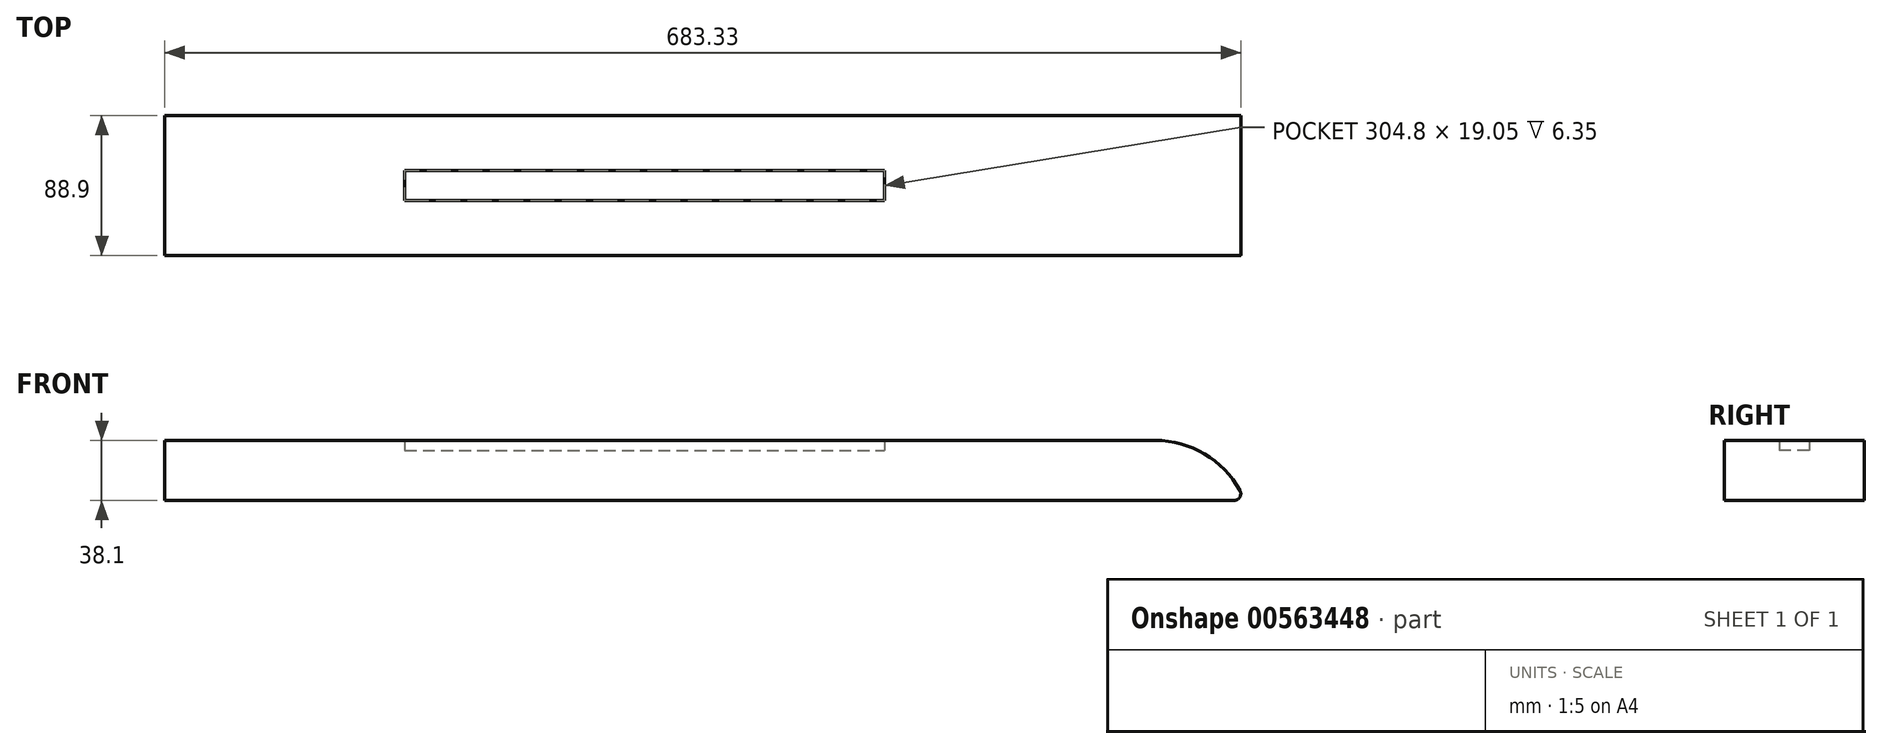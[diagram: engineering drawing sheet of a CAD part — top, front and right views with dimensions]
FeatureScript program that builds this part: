
annotation { "Feature Type Name" : "Feature", "Feature Type Description" : "" }
export const myFeature = defineFeature(function(context is Context, id is Id, definition is map)
    precondition{}
    {
        {
            var Q0;
            Q0=qCreatedBy(makeId("Top.planeOp"),FACE);
            var sketch = newSketch(context, id + "F0", { "sketchPlane" : qUnion([Q0])});
            skLineSegment(sketch, "E0.bottom", {"start": v(-326.86, 50.07) * mm, "end": v(358.94, 50.07) * mm});
            skLineSegment(sketch, "E0.top", {"start": v(-326.86, -38.83) * mm, "end": v(358.94, -38.83) * mm});
            skLineSegment(sketch, "E0.left", {"start": v(-326.86, 50.07) * mm, "end": v(-326.86, -38.83) * mm});
            skLineSegment(sketch, "E0.right", {"start": v(358.94, 50.07) * mm, "end": v(358.94, -38.83) * mm});
            skLineSegment(sketch, "E1.bottom", {"start": v(-174.46, 15.14) * mm, "end": v(130.34, 15.14) * mm});
            skLineSegment(sketch, "E1.top", {"start": v(-174.46, -3.9) * mm, "end": v(130.34, -3.9) * mm});
            skLineSegment(sketch, "E1.left", {"start": v(-174.46, 15.14) * mm, "end": v(-174.46, -3.9) * mm});
            skLineSegment(sketch, "E1.right", {"start": v(130.34, 15.14) * mm, "end": v(130.34, -3.9) * mm});
            skSolve(sketch);
        }
        {
            var Q0;
            Q0=qSketchRegion(id+"F0",true);
            extrude(context, id + "F1", {"entities" : qUnion([Q0]), "depth" : 38.1 * mm, "offsetDistance" : 25.4 * mm});
        }
        {
            var Q0;
            Q0=makeQuery(id+"F1.opExtrude","CAP_EDGE",EDGE,{"disambiguationData":[OSD([sQuery(id+"F0.wireOp",EDGE,"E0.right")])],"isStart":false});
            fillet(context, id + "F2", {"entities" : qUnion([Q0]), "radius" : 61.32 * mm, "tangentPropagation" : true, "allowEdgeOverflow" : false});
        }
        {
            var Q0;
            {var subQ0=sQuery(id+"F0.wireOp",EDGE,"E0.right");Q0=makeQuery(id+"F2.opFillet","BLEND_EDGE",EDGE,{"blendedFrom":[makeQuery(id+"F1.opExtrude","CAP_EDGE",EDGE,{"disambiguationData":[OSD([subQ0])],"isStart":false}),makeQuery(id+"F1.opExtrude","CAP_FACE",FACE,{"disambiguationData":[OSD([sQuery(id+"F0.wireOp",EDGE,"E0.bottom"),sQuery(id+"F0.wireOp",EDGE,"E0.top"),sQuery(id+"F0.wireOp",EDGE,"E0.left"),subQ0])],"isStart":true})],"blendedInto":[makeQuery(id+"F1.opExtrude","CAP_FACE",FACE,{"disambiguationData":[OSD([sQuery(id+"F0.wireOp",EDGE,"E0.bottom"),sQuery(id+"F0.wireOp",EDGE,"E0.top"),sQuery(id+"F0.wireOp",EDGE,"E0.left"),subQ0])],"isStart":true})]});}
            fillet(context, id + "F3", {"entities" : qUnion([Q0]), "radius" : 4.24 * mm, "tangentPropagation" : true, "allowEdgeOverflow" : false});
        }
        {
            var Q0;
            Q0=makeQuery(id+"F0.imprint","IMPRINT",FACE,{"disambiguationData":[TD([[makeQuery(id+"F0.imprint","IMPRINT",EDGE,{"derivedFrom":sQuery(id+"F0.wireOp",EDGE,"E1.bottom")}),-1.0]])]});
            extrude(context, id + "F4", {"entities" : qUnion([Q0]), "operationType" : NewBodyOperationType.ADD, "depth" : 31.75 * mm, "offsetDistance" : 25.4 * mm});
        }
    });
